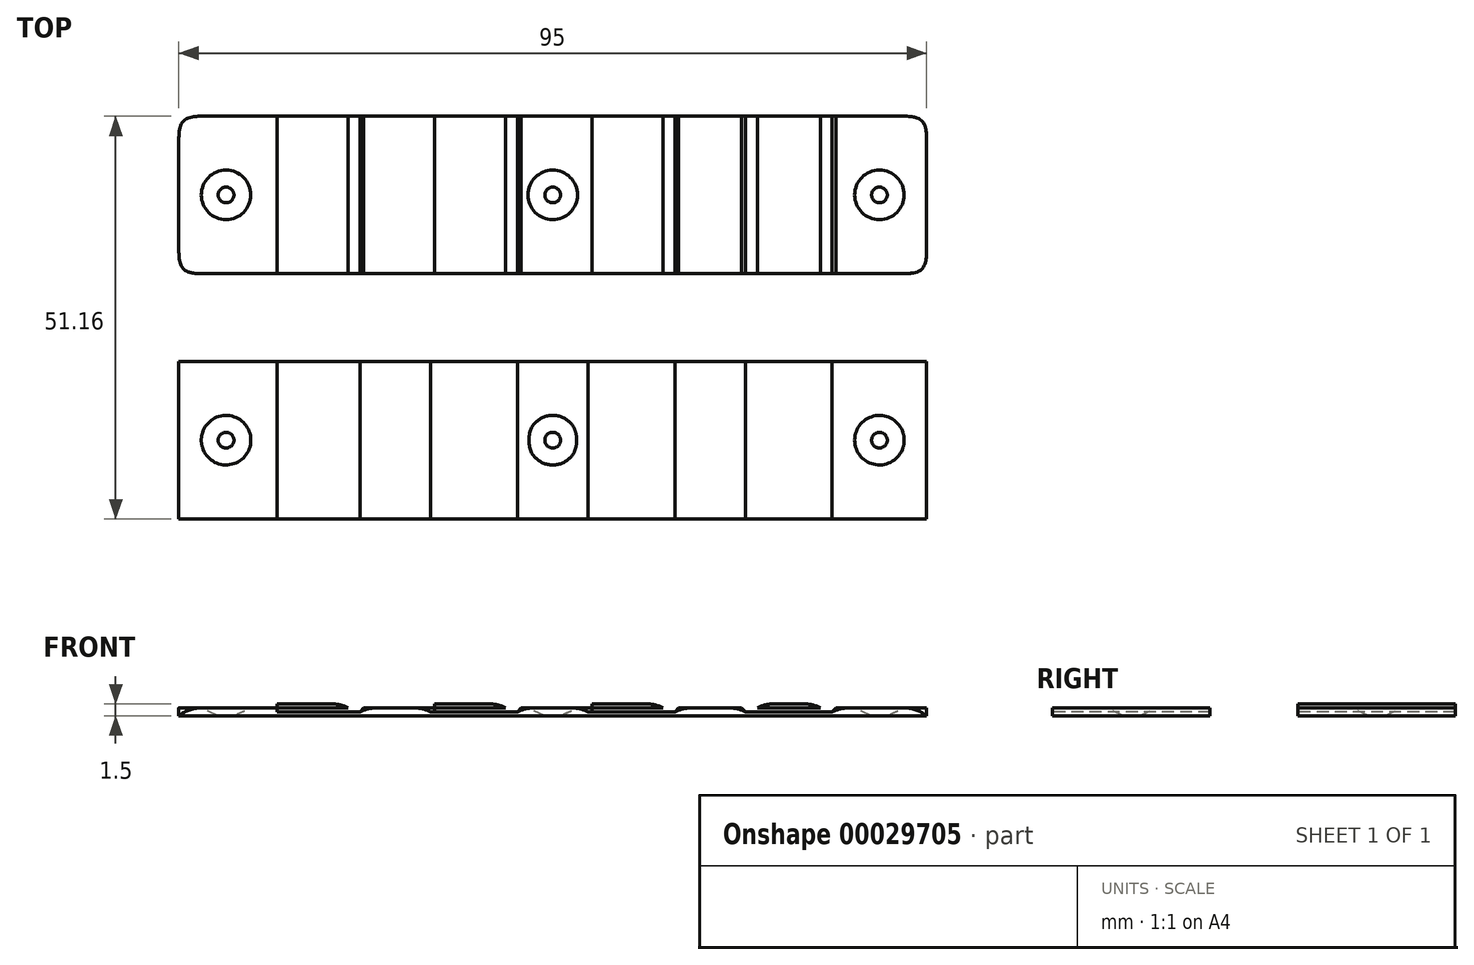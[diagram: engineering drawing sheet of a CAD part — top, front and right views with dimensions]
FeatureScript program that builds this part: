
annotation { "Feature Type Name" : "Feature", "Feature Type Description" : "" }
export const myFeature = defineFeature(function(context is Context, id is Id, definition is map)
    precondition{}
    {
        {
            var Q0;
            Q0=qCreatedBy(makeId("Top.planeOp"),FACE);
            var sketch = newSketch(context, id + "F0", { "sketchPlane" : qUnion([Q0])});
            skLineSegment(sketch, "E0.rect.bottom", {"start": v(47.5, 10) * mm, "end": v(-47.5, 10) * mm});
            skLineSegment(sketch, "E0.rect.top", {"start": v(47.5, -10) * mm, "end": v(-47.5, -10) * mm});
            skLineSegment(sketch, "E0.rect.left", {"start": v(47.5, 10) * mm, "end": v(47.5, -10) * mm});
            skLineSegment(sketch, "E0.rect.right", {"start": v(-47.5, 10) * mm, "end": v(-47.5, -10) * mm});
            skPoint(sketch, "E0.rect.middle", {"position": v(0, 0) * mm});
            skLineSegment(sketch, "E1.bottom", {"start": v(47.5, -21.16) * mm, "end": v(-47.5, -21.16) * mm});
            skLineSegment(sketch, "E1.top", {"start": v(47.5, -41.16) * mm, "end": v(-47.5, -41.16) * mm});
            skLineSegment(sketch, "E1.left", {"start": v(47.5, -21.16) * mm, "end": v(47.5, -41.16) * mm});
            skLineSegment(sketch, "E1.right", {"start": v(-47.5, -21.16) * mm, "end": v(-47.5, -41.16) * mm});
            skCircle(sketch, "E2", {"center": v(0, 0) * mm, "radius": 1 * mm});
            skCircle(sketch, "E3", {"center": v(0, -31.16) * mm, "radius": 1 * mm});
            skPoint(sketch, "E3.centerSnap0", {"position": v(47.5, -31.16) * mm});
            skPoint(sketch, "E3.centerSnap1", {"position": v(0, -41.16) * mm});
            skCircle(sketch, "E4", {"center": v(41.5, 0) * mm, "radius": 1 * mm});
            skCircle(sketch, "E5", {"center": v(41.5, -31.16) * mm, "radius": 1 * mm});
            skCircle(sketch, "E6", {"center": v(-41.5, 0) * mm, "radius": 1 * mm});
            skCircle(sketch, "E7", {"center": v(-41.5, -31.16) * mm, "radius": 1 * mm});
            skPoint(sketch, "E7.centerSnap0", {"position": v(-47.5, -31.16) * mm});
            skSolve(sketch);
        }
        {
            var Q0;
            Q0 = qSketchRegion(id + "F0", true);
            extrude(context, id + "F1", {"entities" : qUnion([Q0]), "depth" : 1 * mm});
        }
        {
            var Q0;
            Q0=makeQuery(id+"F1.opExtrude","CAP_FACE",FACE,{"disambiguationData":[OSD([sQuery(id+"F0.wireOp",EDGE,"E0.rect.bottom"),sQuery(id+"F0.wireOp",EDGE,"E0.rect.top"),sQuery(id+"F0.wireOp",EDGE,"E0.rect.left"),sQuery(id+"F0.wireOp",EDGE,"E0.rect.right"),sQuery(id+"F0.wireOp",EDGE,"E2"),sQuery(id+"F0.wireOp",EDGE,"E4"),sQuery(id+"F0.wireOp",EDGE,"E6")])],"isStart":false});
            var sketch = newSketch(context, id + "F2", { "sketchPlane" : qUnion([Q0])});
            skLineSegment(sketch, "E8.rect.right", {"start": v(-5, 10) * mm, "end": v(-5, -10) * mm});
            skPoint(sketch, "E8.rect.middle", {"position": v(0, 0) * mm});
            skLineSegment(sketch, "E9.bottom", {"start": v(-5, 10) * mm, "end": v(-15, 10) * mm});
            skLineSegment(sketch, "E9.top", {"start": v(-5, -10) * mm, "end": v(-15, -10) * mm});
            skLineSegment(sketch, "E9.right", {"start": v(-15, 10) * mm, "end": v(-15, -10) * mm});
            skLineSegment(sketch, "E10.1.0.0", {"start": v(5, 10) * mm, "end": v(5, -10) * mm});
            skLineSegment(sketch, "E10.1.0.1", {"start": v(15, 10) * mm, "end": v(5, 10) * mm});
            skLineSegment(sketch, "E10.1.0.2", {"start": v(15, 10) * mm, "end": v(15, -10) * mm});
            skLineSegment(sketch, "E10.1.0.3", {"start": v(15, -10) * mm, "end": v(5, -10) * mm});
            skLineSegment(sketch, "E10.2.0.0", {"start": v(25, 10) * mm, "end": v(25, -10) * mm});
            skLineSegment(sketch, "E10.2.0.1", {"start": v(35, 10) * mm, "end": v(25, 10) * mm});
            skLineSegment(sketch, "E10.2.0.2", {"start": v(35, 10) * mm, "end": v(35, -10) * mm});
            skLineSegment(sketch, "E10.2.0.3", {"start": v(35, -10) * mm, "end": v(25, -10) * mm});
            skLineSegment(sketch, "E10.direction1", {"start": v(-15, -10) * mm, "end": v(5, -10) * mm, "construction": true});
            skLineSegment(sketch, "E11.1.0.0", {"start": v(-35, 10) * mm, "end": v(-35, -10) * mm});
            skLineSegment(sketch, "E11.1.0.1", {"start": v(-25, 10) * mm, "end": v(-35, 10) * mm});
            skLineSegment(sketch, "E11.1.0.2", {"start": v(-25, 10) * mm, "end": v(-25, -10) * mm});
            skLineSegment(sketch, "E11.1.0.3", {"start": v(-25, -10) * mm, "end": v(-35, -10) * mm});
            skLineSegment(sketch, "E11.direction1", {"start": v(-15, -10) * mm, "end": v(-35, -10) * mm, "construction": true});
            skLineSegment(sketch, "E12.bottom", {"start": v(-35, -20.93) * mm, "end": v(-25, -20.93) * mm});
            skLineSegment(sketch, "E12.top", {"start": v(-35, -41.22) * mm, "end": v(-25, -41.22) * mm});
            skLineSegment(sketch, "E12.left", {"start": v(-35, -20.93) * mm, "end": v(-35, -41.22) * mm});
            skLineSegment(sketch, "E12.right", {"start": v(-25, -20.93) * mm, "end": v(-25, -41.22) * mm});
            skLineSegment(sketch, "E13.bottom", {"start": v(-15, -21.08) * mm, "end": v(-5, -21.08) * mm});
            skLineSegment(sketch, "E13.top", {"start": v(-15, -41.22) * mm, "end": v(-5, -41.22) * mm});
            skLineSegment(sketch, "E13.left", {"start": v(-15, -21.08) * mm, "end": v(-15, -41.22) * mm});
            skLineSegment(sketch, "E13.right", {"start": v(-5, -21.08) * mm, "end": v(-5, -41.22) * mm});
            skLineSegment(sketch, "E14.bottom", {"start": v(5, -21.04) * mm, "end": v(15, -21.04) * mm});
            skLineSegment(sketch, "E14.top", {"start": v(5, -41.22) * mm, "end": v(15, -41.22) * mm});
            skLineSegment(sketch, "E14.left", {"start": v(5, -21.04) * mm, "end": v(5, -41.22) * mm});
            skLineSegment(sketch, "E14.right", {"start": v(15, -21.04) * mm, "end": v(15, -41.22) * mm});
            skLineSegment(sketch, "E15.bottom", {"start": v(25, -20.8) * mm, "end": v(35, -20.8) * mm});
            skLineSegment(sketch, "E15.top", {"start": v(25, -41.22) * mm, "end": v(35, -41.22) * mm});
            skLineSegment(sketch, "E15.left", {"start": v(25, -20.8) * mm, "end": v(25, -41.22) * mm});
            skLineSegment(sketch, "E15.right", {"start": v(35, -20.8) * mm, "end": v(35, -41.22) * mm});
            skSolve(sketch);
        }
        {
            var Q0;
            Q0=makeQuery(id+"F2.imprint","IMPRINT",FACE,{"disambiguationData":[TD([[makeQuery(id+"F2.imprint","IMPRINT",EDGE,{"derivedFrom":sQuery(id+"F2.wireOp",EDGE,"E8.rect.right")}),-1.0]])]});
            extrude(context, id + "F3", {"entities" : qUnion([Q0]), "operationType" : NewBodyOperationType.ADD, "depth" : .5 * mm});
        }
        {
            var Q0;
            Q0=makeQuery(id+"F2.imprint","IMPRINT",FACE,{"disambiguationData":[TD([[makeQuery(id+"F2.imprint","IMPRINT",EDGE,{"derivedFrom":sQuery(id+"F2.wireOp",EDGE,"E11.1.0.0")}),1.0]])]});
            var Q1;
            Q1=makeQuery(id+"F2.imprint","IMPRINT",FACE,{"disambiguationData":[TD([[makeQuery(id+"F2.imprint","IMPRINT",EDGE,{"derivedFrom":sQuery(id+"F2.wireOp",EDGE,"E10.1.0.0")}),1.0]])]});
            var Q2;
            Q2=makeQuery(id+"F2.imprint","IMPRINT",FACE,{"disambiguationData":[TD([[makeQuery(id+"F2.imprint","IMPRINT",EDGE,{"derivedFrom":sQuery(id+"F2.wireOp",EDGE,"E10.2.0.0")}),1.0]])]});
            extrude(context, id + "F4", {"entities" : qUnion([Q0, Q1, Q2]), "operationType" : NewBodyOperationType.ADD, "depth" : .5 * mm});
        }
        {
            var Q0;
            Q0 = qSketchRegion(id + "F2", true);
            extrude(context, id + "F5", {"entities" : qUnion([Q0]), "operationType" : NewBodyOperationType.REMOVE, "oppositeDirection" : true, "depth" : .5 * mm});
        }
        {
            var Q0;
            Q0=makeQuery(id+"F4.opExtrude","CAP_EDGE",EDGE,{"disambiguationData":[OSD([sQuery(id+"F2.wireOp",EDGE,"E10.2.0.2")])],"isStart":true});
            var Q1;
            Q1=makeQuery(id+"F4.opExtrude","CAP_EDGE",EDGE,{"disambiguationData":[OSD([sQuery(id+"F2.wireOp",EDGE,"E10.1.0.2")])],"isStart":true});
            var Q2;
            Q2=makeQuery(id+"F3.opExtrude","CAP_EDGE",EDGE,{"disambiguationData":[OSD([sQuery(id+"F2.wireOp",EDGE,"E8.rect.right")])],"isStart":true});
            var Q3;
            Q3=makeQuery(id+"F4.opExtrude","CAP_EDGE",EDGE,{"disambiguationData":[OSD([sQuery(id+"F2.wireOp",EDGE,"E11.1.0.2")])],"isStart":true});
            var Q4;
            Q4=makeQuery(id+"F4.opExtrude","CAP_EDGE",EDGE,{"disambiguationData":[OSD([sQuery(id+"F2.wireOp",EDGE,"E11.1.0.0")])],"isStart":true});
            var Q5;
            Q5=makeQuery(id+"F3.opExtrude","CAP_EDGE",EDGE,{"disambiguationData":[OSD([sQuery(id+"F2.wireOp",EDGE,"E9.right")])],"isStart":true});
            var Q6;
            Q6=makeQuery(id+"F4.opExtrude","CAP_EDGE",EDGE,{"disambiguationData":[OSD([sQuery(id+"F2.wireOp",EDGE,"E10.1.0.0")])],"isStart":true});
            var Q7;
            Q7=makeQuery(id+"F4.opExtrude","CAP_EDGE",EDGE,{"disambiguationData":[OSD([sQuery(id+"F2.wireOp",EDGE,"E10.2.0.0")])],"isStart":true});
            var Q8;
            Q8=makeQuery(id+"F5.boolean.opBoolean","COPY",EDGE,{"derivedFrom":makeQuery(id+"F5.opExtrude","CAP_EDGE",EDGE,{"disambiguationData":[OSD([sQuery(id+"F2.wireOp",EDGE,"E12.left")])],"isStart":true})});
            var Q9;
            Q9=makeQuery(id+"F5.boolean.opBoolean","COPY",EDGE,{"derivedFrom":makeQuery(id+"F5.opExtrude","CAP_EDGE",EDGE,{"disambiguationData":[OSD([sQuery(id+"F2.wireOp",EDGE,"E12.right")])],"isStart":true})});
            var Q10;
            Q10=makeQuery(id+"F5.boolean.opBoolean","COPY",EDGE,{"derivedFrom":makeQuery(id+"F5.opExtrude","CAP_EDGE",EDGE,{"disambiguationData":[OSD([sQuery(id+"F2.wireOp",EDGE,"E13.left")])],"isStart":true})});
            var Q11;
            Q11=makeQuery(id+"F5.boolean.opBoolean","COPY",EDGE,{"derivedFrom":makeQuery(id+"F5.opExtrude","CAP_EDGE",EDGE,{"disambiguationData":[OSD([sQuery(id+"F2.wireOp",EDGE,"E13.right")])],"isStart":true})});
            var Q12;
            Q12=makeQuery(id+"F5.boolean.opBoolean","COPY",EDGE,{"derivedFrom":makeQuery(id+"F5.opExtrude","CAP_EDGE",EDGE,{"disambiguationData":[OSD([sQuery(id+"F2.wireOp",EDGE,"E14.left")])],"isStart":true})});
            var Q13;
            Q13=makeQuery(id+"F5.boolean.opBoolean","COPY",EDGE,{"derivedFrom":makeQuery(id+"F5.opExtrude","CAP_EDGE",EDGE,{"disambiguationData":[OSD([sQuery(id+"F2.wireOp",EDGE,"E14.right")])],"isStart":true})});
            var Q14;
            Q14=makeQuery(id+"F5.boolean.opBoolean","COPY",EDGE,{"derivedFrom":makeQuery(id+"F5.opExtrude","CAP_EDGE",EDGE,{"disambiguationData":[OSD([sQuery(id+"F2.wireOp",EDGE,"E15.left")])],"isStart":true})});
            var Q15;
            Q15=makeQuery(id+"F5.boolean.opBoolean","COPY",EDGE,{"derivedFrom":makeQuery(id+"F5.opExtrude","CAP_EDGE",EDGE,{"disambiguationData":[OSD([sQuery(id+"F2.wireOp",EDGE,"E15.right")])],"isStart":true})});
            var Q16;
            Q16=makeQuery(id+"F1.opExtrude","CAP_EDGE",EDGE,{"disambiguationData":[OSD([sQuery(id+"F0.wireOp",EDGE,"E1.right")])],"isStart":false});
            var Q17;
            Q17=makeQuery(id+"F1.opExtrude","CAP_EDGE",EDGE,{"disambiguationData":[OSD([sQuery(id+"F0.wireOp",EDGE,"E1.left")])],"isStart":false});
            chamfer(context, id + "F6", {"entities" : qUnion([Q0, Q1, Q2, Q3, Q4, Q5, Q6, Q7, Q8, Q9, Q10, Q11, Q12, Q13, Q14, Q15, Q16, Q17]), "width" : 1 * mm, "tangentPropagation" : true});
        }
        {
            var Q0;
            Q0=makeQuery(id+"F1.opExtrude","SWEPT_EDGE",EDGE,{"disambiguationData":[OSD([sQuery(id+"F0.wireOp",EDGE,"E0.rect.bottom"),sQuery(id+"F0.wireOp",EDGE,"E0.rect.left")])]});
            var Q1;
            Q1=makeQuery(id+"F1.opExtrude","SWEPT_EDGE",EDGE,{"disambiguationData":[OSD([sQuery(id+"F0.wireOp",EDGE,"E0.rect.top"),sQuery(id+"F0.wireOp",EDGE,"E0.rect.left")])]});
            var Q2;
            Q2=makeQuery(id+"F1.opExtrude","SWEPT_EDGE",EDGE,{"disambiguationData":[OSD([sQuery(id+"F0.wireOp",EDGE,"E1.bottom"),sQuery(id+"F0.wireOp",EDGE,"E1.left")])]});
            var Q3;
            Q3=makeQuery(id+"F1.opExtrude","SWEPT_EDGE",EDGE,{"disambiguationData":[OSD([sQuery(id+"F0.wireOp",EDGE,"E0.rect.bottom"),sQuery(id+"F0.wireOp",EDGE,"E0.rect.right")])]});
            var Q4;
            Q4=makeQuery(id+"F1.opExtrude","SWEPT_EDGE",EDGE,{"disambiguationData":[OSD([sQuery(id+"F0.wireOp",EDGE,"E0.rect.top"),sQuery(id+"F0.wireOp",EDGE,"E0.rect.right")])]});
            var Q5;
            Q5=makeQuery(id+"F1.opExtrude","SWEPT_EDGE",EDGE,{"disambiguationData":[OSD([sQuery(id+"F0.wireOp",EDGE,"E1.bottom"),sQuery(id+"F0.wireOp",EDGE,"E1.right")])]});
            var Q6;
            Q6=makeQuery(id+"F1.opExtrude","SWEPT_EDGE",EDGE,{"disambiguationData":[OSD([sQuery(id+"F0.wireOp",EDGE,"E1.top"),sQuery(id+"F0.wireOp",EDGE,"E1.right")])]});
            var Q7;
            Q7=makeQuery(id+"F1.opExtrude","SWEPT_EDGE",EDGE,{"disambiguationData":[OSD([sQuery(id+"F0.wireOp",EDGE,"E1.top"),sQuery(id+"F0.wireOp",EDGE,"E1.left")])]});
            fillet(context, id + "F7", {"entities" : qUnion([Q0, Q1, Q2, Q3, Q4, Q5, Q6, Q7]), "radius" : 3 * mm, "tangentPropagation" : true, "rho" : 0.6, "crossSection" : FilletCrossSection.CONIC, "allowEdgeOverflow" : false});
        }
        {
            var Q0;
            Q0=makeQuery(id+"F1.opExtrude","CAP_EDGE",EDGE,{"disambiguationData":[OSD([sQuery(id+"F0.wireOp",EDGE,"E6")])],"isStart":false});
            var Q1;
            Q1=makeQuery(id+"F1.opExtrude","CAP_EDGE",EDGE,{"disambiguationData":[OSD([sQuery(id+"F0.wireOp",EDGE,"E2")])],"isStart":false});
            var Q2;
            Q2=makeQuery(id+"F1.opExtrude","CAP_EDGE",EDGE,{"disambiguationData":[OSD([sQuery(id+"F0.wireOp",EDGE,"E4")])],"isStart":false});
            var Q3;
            Q3=makeQuery(id+"F1.opExtrude","CAP_EDGE",EDGE,{"disambiguationData":[OSD([sQuery(id+"F0.wireOp",EDGE,"E7")])],"isStart":false});
            var Q4;
            Q4=makeQuery(id+"F1.opExtrude","CAP_EDGE",EDGE,{"disambiguationData":[OSD([sQuery(id+"F0.wireOp",EDGE,"E3")])],"isStart":false});
            var Q5;
            Q5=makeQuery(id+"F1.opExtrude","CAP_EDGE",EDGE,{"disambiguationData":[OSD([sQuery(id+"F0.wireOp",EDGE,"E5")])],"isStart":false});
            chamfer(context, id + "F8", {"entities" : qUnion([Q0, Q1, Q2, Q3, Q4, Q5]), "chamferType" : ChamferType.OFFSET_ANGLE, "width" : 1 * mm, "oppositeDirection" : false, "angle" : 65 * degree, "tangentPropagation" : true});
        }
        {
            var Q0;
            {var subQ0=sQuery(id+"F2.wireOp",EDGE,"E11.1.0.0");Q0=makeQuery(id+"F6.opChamfer","BLEND_EDGE",EDGE,{"blendedFrom":[makeQuery(id+"F4.opExtrude","CAP_EDGE",EDGE,{"disambiguationData":[OSD([subQ0])],"isStart":true}),makeQuery(id+"F4.opExtrude","CAP_FACE",FACE,{"disambiguationData":[OSD([subQ0,sQuery(id+"F2.wireOp",EDGE,"E11.1.0.1"),sQuery(id+"F2.wireOp",EDGE,"E11.1.0.2"),sQuery(id+"F2.wireOp",EDGE,"E11.1.0.3")])],"isStart":false})],"blendedInto":[makeQuery(id+"F4.opExtrude","CAP_FACE",FACE,{"disambiguationData":[OSD([subQ0,sQuery(id+"F2.wireOp",EDGE,"E11.1.0.1"),sQuery(id+"F2.wireOp",EDGE,"E11.1.0.2"),sQuery(id+"F2.wireOp",EDGE,"E11.1.0.3")])],"isStart":false})]});}
            var Q1;
            {var subQ0=sQuery(id+"F2.wireOp",EDGE,"E11.1.0.2");Q1=makeQuery(id+"F6.opChamfer","BLEND_EDGE",EDGE,{"blendedFrom":[makeQuery(id+"F4.opExtrude","CAP_EDGE",EDGE,{"disambiguationData":[OSD([subQ0])],"isStart":true}),makeQuery(id+"F4.opExtrude","CAP_FACE",FACE,{"disambiguationData":[OSD([sQuery(id+"F2.wireOp",EDGE,"E11.1.0.0"),sQuery(id+"F2.wireOp",EDGE,"E11.1.0.1"),subQ0,sQuery(id+"F2.wireOp",EDGE,"E11.1.0.3")])],"isStart":false})],"blendedInto":[makeQuery(id+"F4.opExtrude","CAP_FACE",FACE,{"disambiguationData":[OSD([sQuery(id+"F2.wireOp",EDGE,"E11.1.0.0"),sQuery(id+"F2.wireOp",EDGE,"E11.1.0.1"),subQ0,sQuery(id+"F2.wireOp",EDGE,"E11.1.0.3")])],"isStart":false})]});}
            var Q2;
            {var subQ0=sQuery(id+"F2.wireOp",EDGE,"E9.right");Q2=makeQuery(id+"F6.opChamfer","BLEND_EDGE",EDGE,{"blendedFrom":[makeQuery(id+"F3.opExtrude","CAP_EDGE",EDGE,{"disambiguationData":[OSD([subQ0])],"isStart":true}),makeQuery(id+"F3.opExtrude","CAP_FACE",FACE,{"disambiguationData":[OSD([sQuery(id+"F2.wireOp",EDGE,"E8.rect.right"),sQuery(id+"F2.wireOp",EDGE,"E9.bottom"),sQuery(id+"F2.wireOp",EDGE,"E9.top"),subQ0])],"isStart":false})],"blendedInto":[makeQuery(id+"F3.opExtrude","CAP_FACE",FACE,{"disambiguationData":[OSD([sQuery(id+"F2.wireOp",EDGE,"E8.rect.right"),sQuery(id+"F2.wireOp",EDGE,"E9.bottom"),sQuery(id+"F2.wireOp",EDGE,"E9.top"),subQ0])],"isStart":false})]});}
            var Q3;
            {var subQ0=sQuery(id+"F2.wireOp",EDGE,"E8.rect.right");Q3=makeQuery(id+"F6.opChamfer","BLEND_EDGE",EDGE,{"blendedFrom":[makeQuery(id+"F3.opExtrude","CAP_EDGE",EDGE,{"disambiguationData":[OSD([subQ0])],"isStart":true}),makeQuery(id+"F3.opExtrude","CAP_FACE",FACE,{"disambiguationData":[OSD([subQ0,sQuery(id+"F2.wireOp",EDGE,"E9.bottom"),sQuery(id+"F2.wireOp",EDGE,"E9.top"),sQuery(id+"F2.wireOp",EDGE,"E9.right")])],"isStart":false})],"blendedInto":[makeQuery(id+"F3.opExtrude","CAP_FACE",FACE,{"disambiguationData":[OSD([subQ0,sQuery(id+"F2.wireOp",EDGE,"E9.bottom"),sQuery(id+"F2.wireOp",EDGE,"E9.top"),sQuery(id+"F2.wireOp",EDGE,"E9.right")])],"isStart":false})]});}
            var Q4;
            {var subQ0=sQuery(id+"F2.wireOp",EDGE,"E10.1.0.0");Q4=makeQuery(id+"F6.opChamfer","BLEND_EDGE",EDGE,{"blendedFrom":[makeQuery(id+"F4.opExtrude","CAP_EDGE",EDGE,{"disambiguationData":[OSD([subQ0])],"isStart":true}),makeQuery(id+"F4.opExtrude","CAP_FACE",FACE,{"disambiguationData":[OSD([subQ0,sQuery(id+"F2.wireOp",EDGE,"E10.1.0.1"),sQuery(id+"F2.wireOp",EDGE,"E10.1.0.2"),sQuery(id+"F2.wireOp",EDGE,"E10.1.0.3")])],"isStart":false})],"blendedInto":[makeQuery(id+"F4.opExtrude","CAP_FACE",FACE,{"disambiguationData":[OSD([subQ0,sQuery(id+"F2.wireOp",EDGE,"E10.1.0.1"),sQuery(id+"F2.wireOp",EDGE,"E10.1.0.2"),sQuery(id+"F2.wireOp",EDGE,"E10.1.0.3")])],"isStart":false})]});}
            var Q5;
            {var subQ0=sQuery(id+"F2.wireOp",EDGE,"E10.1.0.2");Q5=makeQuery(id+"F6.opChamfer","BLEND_EDGE",EDGE,{"blendedFrom":[makeQuery(id+"F4.opExtrude","CAP_EDGE",EDGE,{"disambiguationData":[OSD([subQ0])],"isStart":true}),makeQuery(id+"F4.opExtrude","CAP_FACE",FACE,{"disambiguationData":[OSD([sQuery(id+"F2.wireOp",EDGE,"E10.1.0.0"),sQuery(id+"F2.wireOp",EDGE,"E10.1.0.1"),subQ0,sQuery(id+"F2.wireOp",EDGE,"E10.1.0.3")])],"isStart":false})],"blendedInto":[makeQuery(id+"F4.opExtrude","CAP_FACE",FACE,{"disambiguationData":[OSD([sQuery(id+"F2.wireOp",EDGE,"E10.1.0.0"),sQuery(id+"F2.wireOp",EDGE,"E10.1.0.1"),subQ0,sQuery(id+"F2.wireOp",EDGE,"E10.1.0.3")])],"isStart":false})]});}
            var Q6;
            {var subQ0=sQuery(id+"F2.wireOp",EDGE,"E10.2.0.0");Q6=makeQuery(id+"F6.opChamfer","BLEND_EDGE",EDGE,{"blendedFrom":[makeQuery(id+"F4.opExtrude","CAP_EDGE",EDGE,{"disambiguationData":[OSD([subQ0])],"isStart":true}),makeQuery(id+"F4.opExtrude","CAP_FACE",FACE,{"disambiguationData":[OSD([subQ0,sQuery(id+"F2.wireOp",EDGE,"E10.2.0.1"),sQuery(id+"F2.wireOp",EDGE,"E10.2.0.2"),sQuery(id+"F2.wireOp",EDGE,"E10.2.0.3")])],"isStart":false})],"blendedInto":[makeQuery(id+"F4.opExtrude","CAP_FACE",FACE,{"disambiguationData":[OSD([subQ0,sQuery(id+"F2.wireOp",EDGE,"E10.2.0.1"),sQuery(id+"F2.wireOp",EDGE,"E10.2.0.2"),sQuery(id+"F2.wireOp",EDGE,"E10.2.0.3")])],"isStart":false})]});}
            var Q7;
            {var subQ0=sQuery(id+"F2.wireOp",EDGE,"E10.2.0.2");Q7=makeQuery(id+"F6.opChamfer","BLEND_EDGE",EDGE,{"blendedFrom":[makeQuery(id+"F4.opExtrude","CAP_EDGE",EDGE,{"disambiguationData":[OSD([subQ0])],"isStart":true}),makeQuery(id+"F4.opExtrude","CAP_FACE",FACE,{"disambiguationData":[OSD([sQuery(id+"F2.wireOp",EDGE,"E10.2.0.0"),sQuery(id+"F2.wireOp",EDGE,"E10.2.0.1"),subQ0,sQuery(id+"F2.wireOp",EDGE,"E10.2.0.3")])],"isStart":false})],"blendedInto":[makeQuery(id+"F4.opExtrude","CAP_FACE",FACE,{"disambiguationData":[OSD([sQuery(id+"F2.wireOp",EDGE,"E10.2.0.0"),sQuery(id+"F2.wireOp",EDGE,"E10.2.0.1"),subQ0,sQuery(id+"F2.wireOp",EDGE,"E10.2.0.3")])],"isStart":false})]});}
            var Q8;
            {var subQ0=sQuery(id+"F2.wireOp",EDGE,"E15.right");var subQ1=sQuery(id+"F0.wireOp",EDGE,"E1.bottom");var subQ2=sQuery(id+"F0.wireOp",EDGE,"E1.top");var subQ3=sQuery(id+"F0.wireOp",EDGE,"E1.left");var subQ4=sQuery(id+"F0.wireOp",EDGE,"E5");Q8=makeQuery(id+"F6.opChamfer","BLEND_EDGE",EDGE,{"blendedFrom":[makeQuery(id+"F5.boolean.opBoolean","COPY",EDGE,{"derivedFrom":makeQuery(id+"F5.opExtrude","CAP_EDGE",EDGE,{"disambiguationData":[OSD([subQ0])],"isStart":true})}),makeQuery(id+"F5.boolean.opBoolean","SPLIT",FACE,{"disambiguationData":[TD([makeQuery(id+"F1.opExtrude","SWEPT_FACE",FACE,{"disambiguationData":[OSD([subQ3])]})])],"derivedFrom":makeQuery(id+"F1.opExtrude","CAP_FACE",FACE,{"disambiguationData":[OSD([subQ1,subQ2,subQ3,sQuery(id+"F0.wireOp",EDGE,"E1.right"),sQuery(id+"F0.wireOp",EDGE,"E3"),subQ4,sQuery(id+"F0.wireOp",EDGE,"E7")])],"isStart":false})})],"blendedInto":[makeQuery(id+"F5.boolean.opBoolean","SPLIT",FACE,{"disambiguationData":[TD([makeQuery(id+"F1.opExtrude","SWEPT_FACE",FACE,{"disambiguationData":[OSD([subQ3])]})])],"derivedFrom":makeQuery(id+"F1.opExtrude","CAP_FACE",FACE,{"disambiguationData":[OSD([subQ1,subQ2,subQ3,sQuery(id+"F0.wireOp",EDGE,"E1.right"),sQuery(id+"F0.wireOp",EDGE,"E3"),subQ4,sQuery(id+"F0.wireOp",EDGE,"E7")])],"isStart":false})})]});}
            var Q9;
            {var subQ0=sQuery(id+"F2.wireOp",EDGE,"E15.left");var subQ1=sQuery(id+"F0.wireOp",EDGE,"E1.bottom");var subQ2=sQuery(id+"F0.wireOp",EDGE,"E1.top");Q9=makeQuery(id+"F6.opChamfer","BLEND_EDGE",EDGE,{"blendedFrom":[makeQuery(id+"F5.boolean.opBoolean","COPY",EDGE,{"derivedFrom":makeQuery(id+"F5.opExtrude","CAP_EDGE",EDGE,{"disambiguationData":[OSD([subQ0])],"isStart":true})}),makeQuery(id+"F5.boolean.opBoolean","SPLIT",FACE,{"disambiguationData":[TD([makeQuery(id+"F5.opExtrude","SWEPT_FACE",FACE,{"disambiguationData":[OSD([sQuery(id+"F2.wireOp",EDGE,"E14.right")])]})])],"derivedFrom":makeQuery(id+"F1.opExtrude","CAP_FACE",FACE,{"disambiguationData":[OSD([subQ1,subQ2,sQuery(id+"F0.wireOp",EDGE,"E1.left"),sQuery(id+"F0.wireOp",EDGE,"E1.right"),sQuery(id+"F0.wireOp",EDGE,"E3"),sQuery(id+"F0.wireOp",EDGE,"E5"),sQuery(id+"F0.wireOp",EDGE,"E7")])],"isStart":false})})],"blendedInto":[makeQuery(id+"F5.boolean.opBoolean","SPLIT",FACE,{"disambiguationData":[TD([makeQuery(id+"F5.opExtrude","SWEPT_FACE",FACE,{"disambiguationData":[OSD([sQuery(id+"F2.wireOp",EDGE,"E14.right")])]})])],"derivedFrom":makeQuery(id+"F1.opExtrude","CAP_FACE",FACE,{"disambiguationData":[OSD([subQ1,subQ2,sQuery(id+"F0.wireOp",EDGE,"E1.left"),sQuery(id+"F0.wireOp",EDGE,"E1.right"),sQuery(id+"F0.wireOp",EDGE,"E3"),sQuery(id+"F0.wireOp",EDGE,"E5"),sQuery(id+"F0.wireOp",EDGE,"E7")])],"isStart":false})})]});}
            var Q10;
            {var subQ0=sQuery(id+"F2.wireOp",EDGE,"E14.right");var subQ1=sQuery(id+"F0.wireOp",EDGE,"E1.bottom");var subQ2=sQuery(id+"F0.wireOp",EDGE,"E1.top");Q10=makeQuery(id+"F6.opChamfer","BLEND_EDGE",EDGE,{"blendedFrom":[makeQuery(id+"F5.boolean.opBoolean","COPY",EDGE,{"derivedFrom":makeQuery(id+"F5.opExtrude","CAP_EDGE",EDGE,{"disambiguationData":[OSD([subQ0])],"isStart":true})}),makeQuery(id+"F5.boolean.opBoolean","SPLIT",FACE,{"disambiguationData":[TD([makeQuery(id+"F5.opExtrude","SWEPT_FACE",FACE,{"disambiguationData":[OSD([subQ0])]})])],"derivedFrom":makeQuery(id+"F1.opExtrude","CAP_FACE",FACE,{"disambiguationData":[OSD([subQ1,subQ2,sQuery(id+"F0.wireOp",EDGE,"E1.left"),sQuery(id+"F0.wireOp",EDGE,"E1.right"),sQuery(id+"F0.wireOp",EDGE,"E3"),sQuery(id+"F0.wireOp",EDGE,"E5"),sQuery(id+"F0.wireOp",EDGE,"E7")])],"isStart":false})})],"blendedInto":[makeQuery(id+"F5.boolean.opBoolean","SPLIT",FACE,{"disambiguationData":[TD([makeQuery(id+"F5.opExtrude","SWEPT_FACE",FACE,{"disambiguationData":[OSD([subQ0])]})])],"derivedFrom":makeQuery(id+"F1.opExtrude","CAP_FACE",FACE,{"disambiguationData":[OSD([subQ1,subQ2,sQuery(id+"F0.wireOp",EDGE,"E1.left"),sQuery(id+"F0.wireOp",EDGE,"E1.right"),sQuery(id+"F0.wireOp",EDGE,"E3"),sQuery(id+"F0.wireOp",EDGE,"E5"),sQuery(id+"F0.wireOp",EDGE,"E7")])],"isStart":false})})]});}
            var Q11;
            {var subQ0=sQuery(id+"F2.wireOp",EDGE,"E14.left");var subQ1=sQuery(id+"F0.wireOp",EDGE,"E1.bottom");var subQ2=sQuery(id+"F0.wireOp",EDGE,"E1.top");var subQ3=sQuery(id+"F0.wireOp",EDGE,"E3");Q11=makeQuery(id+"F6.opChamfer","BLEND_EDGE",EDGE,{"blendedFrom":[makeQuery(id+"F5.boolean.opBoolean","COPY",EDGE,{"derivedFrom":makeQuery(id+"F5.opExtrude","CAP_EDGE",EDGE,{"disambiguationData":[OSD([subQ0])],"isStart":true})}),makeQuery(id+"F5.boolean.opBoolean","SPLIT",FACE,{"disambiguationData":[TD([makeQuery(id+"F1.opExtrude","SWEPT_FACE",FACE,{"disambiguationData":[OSD([subQ3])]})])],"derivedFrom":makeQuery(id+"F1.opExtrude","CAP_FACE",FACE,{"disambiguationData":[OSD([subQ1,subQ2,sQuery(id+"F0.wireOp",EDGE,"E1.left"),sQuery(id+"F0.wireOp",EDGE,"E1.right"),subQ3,sQuery(id+"F0.wireOp",EDGE,"E5"),sQuery(id+"F0.wireOp",EDGE,"E7")])],"isStart":false})})],"blendedInto":[makeQuery(id+"F5.boolean.opBoolean","SPLIT",FACE,{"disambiguationData":[TD([makeQuery(id+"F1.opExtrude","SWEPT_FACE",FACE,{"disambiguationData":[OSD([subQ3])]})])],"derivedFrom":makeQuery(id+"F1.opExtrude","CAP_FACE",FACE,{"disambiguationData":[OSD([subQ1,subQ2,sQuery(id+"F0.wireOp",EDGE,"E1.left"),sQuery(id+"F0.wireOp",EDGE,"E1.right"),subQ3,sQuery(id+"F0.wireOp",EDGE,"E5"),sQuery(id+"F0.wireOp",EDGE,"E7")])],"isStart":false})})]});}
            var Q12;
            {var subQ0=sQuery(id+"F2.wireOp",EDGE,"E13.right");var subQ1=sQuery(id+"F0.wireOp",EDGE,"E1.bottom");var subQ2=sQuery(id+"F0.wireOp",EDGE,"E1.top");var subQ3=sQuery(id+"F0.wireOp",EDGE,"E3");Q12=makeQuery(id+"F6.opChamfer","BLEND_EDGE",EDGE,{"blendedFrom":[makeQuery(id+"F5.boolean.opBoolean","COPY",EDGE,{"derivedFrom":makeQuery(id+"F5.opExtrude","CAP_EDGE",EDGE,{"disambiguationData":[OSD([subQ0])],"isStart":true})}),makeQuery(id+"F5.boolean.opBoolean","SPLIT",FACE,{"disambiguationData":[TD([makeQuery(id+"F1.opExtrude","SWEPT_FACE",FACE,{"disambiguationData":[OSD([subQ3])]})])],"derivedFrom":makeQuery(id+"F1.opExtrude","CAP_FACE",FACE,{"disambiguationData":[OSD([subQ1,subQ2,sQuery(id+"F0.wireOp",EDGE,"E1.left"),sQuery(id+"F0.wireOp",EDGE,"E1.right"),subQ3,sQuery(id+"F0.wireOp",EDGE,"E5"),sQuery(id+"F0.wireOp",EDGE,"E7")])],"isStart":false})})],"blendedInto":[makeQuery(id+"F5.boolean.opBoolean","SPLIT",FACE,{"disambiguationData":[TD([makeQuery(id+"F1.opExtrude","SWEPT_FACE",FACE,{"disambiguationData":[OSD([subQ3])]})])],"derivedFrom":makeQuery(id+"F1.opExtrude","CAP_FACE",FACE,{"disambiguationData":[OSD([subQ1,subQ2,sQuery(id+"F0.wireOp",EDGE,"E1.left"),sQuery(id+"F0.wireOp",EDGE,"E1.right"),subQ3,sQuery(id+"F0.wireOp",EDGE,"E5"),sQuery(id+"F0.wireOp",EDGE,"E7")])],"isStart":false})})]});}
            var Q13;
            {var subQ0=sQuery(id+"F2.wireOp",EDGE,"E13.left");var subQ1=sQuery(id+"F0.wireOp",EDGE,"E1.bottom");var subQ2=sQuery(id+"F0.wireOp",EDGE,"E1.top");Q13=makeQuery(id+"F6.opChamfer","BLEND_EDGE",EDGE,{"blendedFrom":[makeQuery(id+"F5.boolean.opBoolean","COPY",EDGE,{"derivedFrom":makeQuery(id+"F5.opExtrude","CAP_EDGE",EDGE,{"disambiguationData":[OSD([subQ0])],"isStart":true})}),makeQuery(id+"F5.boolean.opBoolean","SPLIT",FACE,{"disambiguationData":[TD([makeQuery(id+"F5.opExtrude","SWEPT_FACE",FACE,{"disambiguationData":[OSD([sQuery(id+"F2.wireOp",EDGE,"E12.right")])]})])],"derivedFrom":makeQuery(id+"F1.opExtrude","CAP_FACE",FACE,{"disambiguationData":[OSD([subQ1,subQ2,sQuery(id+"F0.wireOp",EDGE,"E1.left"),sQuery(id+"F0.wireOp",EDGE,"E1.right"),sQuery(id+"F0.wireOp",EDGE,"E3"),sQuery(id+"F0.wireOp",EDGE,"E5"),sQuery(id+"F0.wireOp",EDGE,"E7")])],"isStart":false})})],"blendedInto":[makeQuery(id+"F5.boolean.opBoolean","SPLIT",FACE,{"disambiguationData":[TD([makeQuery(id+"F5.opExtrude","SWEPT_FACE",FACE,{"disambiguationData":[OSD([sQuery(id+"F2.wireOp",EDGE,"E12.right")])]})])],"derivedFrom":makeQuery(id+"F1.opExtrude","CAP_FACE",FACE,{"disambiguationData":[OSD([subQ1,subQ2,sQuery(id+"F0.wireOp",EDGE,"E1.left"),sQuery(id+"F0.wireOp",EDGE,"E1.right"),sQuery(id+"F0.wireOp",EDGE,"E3"),sQuery(id+"F0.wireOp",EDGE,"E5"),sQuery(id+"F0.wireOp",EDGE,"E7")])],"isStart":false})})]});}
            var Q14;
            {var subQ0=sQuery(id+"F2.wireOp",EDGE,"E12.right");var subQ1=sQuery(id+"F0.wireOp",EDGE,"E1.bottom");var subQ2=sQuery(id+"F0.wireOp",EDGE,"E1.top");Q14=makeQuery(id+"F6.opChamfer","BLEND_EDGE",EDGE,{"blendedFrom":[makeQuery(id+"F5.boolean.opBoolean","COPY",EDGE,{"derivedFrom":makeQuery(id+"F5.opExtrude","CAP_EDGE",EDGE,{"disambiguationData":[OSD([subQ0])],"isStart":true})}),makeQuery(id+"F5.boolean.opBoolean","SPLIT",FACE,{"disambiguationData":[TD([makeQuery(id+"F5.opExtrude","SWEPT_FACE",FACE,{"disambiguationData":[OSD([subQ0])]})])],"derivedFrom":makeQuery(id+"F1.opExtrude","CAP_FACE",FACE,{"disambiguationData":[OSD([subQ1,subQ2,sQuery(id+"F0.wireOp",EDGE,"E1.left"),sQuery(id+"F0.wireOp",EDGE,"E1.right"),sQuery(id+"F0.wireOp",EDGE,"E3"),sQuery(id+"F0.wireOp",EDGE,"E5"),sQuery(id+"F0.wireOp",EDGE,"E7")])],"isStart":false})})],"blendedInto":[makeQuery(id+"F5.boolean.opBoolean","SPLIT",FACE,{"disambiguationData":[TD([makeQuery(id+"F5.opExtrude","SWEPT_FACE",FACE,{"disambiguationData":[OSD([subQ0])]})])],"derivedFrom":makeQuery(id+"F1.opExtrude","CAP_FACE",FACE,{"disambiguationData":[OSD([subQ1,subQ2,sQuery(id+"F0.wireOp",EDGE,"E1.left"),sQuery(id+"F0.wireOp",EDGE,"E1.right"),sQuery(id+"F0.wireOp",EDGE,"E3"),sQuery(id+"F0.wireOp",EDGE,"E5"),sQuery(id+"F0.wireOp",EDGE,"E7")])],"isStart":false})})]});}
            var Q15;
            {var subQ0=sQuery(id+"F2.wireOp",EDGE,"E12.left");var subQ1=sQuery(id+"F0.wireOp",EDGE,"E1.bottom");var subQ2=sQuery(id+"F0.wireOp",EDGE,"E1.top");var subQ3=sQuery(id+"F0.wireOp",EDGE,"E1.right");var subQ4=sQuery(id+"F0.wireOp",EDGE,"E7");Q15=makeQuery(id+"F6.opChamfer","BLEND_EDGE",EDGE,{"blendedFrom":[makeQuery(id+"F5.boolean.opBoolean","COPY",EDGE,{"derivedFrom":makeQuery(id+"F5.opExtrude","CAP_EDGE",EDGE,{"disambiguationData":[OSD([subQ0])],"isStart":true})}),makeQuery(id+"F5.boolean.opBoolean","SPLIT",FACE,{"disambiguationData":[TD([makeQuery(id+"F1.opExtrude","SWEPT_FACE",FACE,{"disambiguationData":[OSD([subQ3])]})])],"derivedFrom":makeQuery(id+"F1.opExtrude","CAP_FACE",FACE,{"disambiguationData":[OSD([subQ1,subQ2,sQuery(id+"F0.wireOp",EDGE,"E1.left"),subQ3,sQuery(id+"F0.wireOp",EDGE,"E3"),sQuery(id+"F0.wireOp",EDGE,"E5"),subQ4])],"isStart":false})})],"blendedInto":[makeQuery(id+"F5.boolean.opBoolean","SPLIT",FACE,{"disambiguationData":[TD([makeQuery(id+"F1.opExtrude","SWEPT_FACE",FACE,{"disambiguationData":[OSD([subQ3])]})])],"derivedFrom":makeQuery(id+"F1.opExtrude","CAP_FACE",FACE,{"disambiguationData":[OSD([subQ1,subQ2,sQuery(id+"F0.wireOp",EDGE,"E1.left"),subQ3,sQuery(id+"F0.wireOp",EDGE,"E3"),sQuery(id+"F0.wireOp",EDGE,"E5"),subQ4])],"isStart":false})})]});}
            var Q16;
            {var subQ0=sQuery(id+"F0.wireOp",EDGE,"E1.right");var subQ1=sQuery(id+"F0.wireOp",EDGE,"E1.bottom");var subQ2=sQuery(id+"F0.wireOp",EDGE,"E1.top");var subQ3=sQuery(id+"F0.wireOp",EDGE,"E7");Q16=makeQuery(id+"F6.opChamfer","BLEND_EDGE",EDGE,{"blendedFrom":[makeQuery(id+"F1.opExtrude","CAP_EDGE",EDGE,{"disambiguationData":[OSD([subQ0])],"isStart":false}),makeQuery(id+"F5.boolean.opBoolean","SPLIT",FACE,{"disambiguationData":[TD([makeQuery(id+"F1.opExtrude","SWEPT_FACE",FACE,{"disambiguationData":[OSD([subQ0])]})])],"derivedFrom":makeQuery(id+"F1.opExtrude","CAP_FACE",FACE,{"disambiguationData":[OSD([subQ1,subQ2,sQuery(id+"F0.wireOp",EDGE,"E1.left"),subQ0,sQuery(id+"F0.wireOp",EDGE,"E3"),sQuery(id+"F0.wireOp",EDGE,"E5"),subQ3])],"isStart":false})})],"blendedInto":[makeQuery(id+"F5.boolean.opBoolean","SPLIT",FACE,{"disambiguationData":[TD([makeQuery(id+"F1.opExtrude","SWEPT_FACE",FACE,{"disambiguationData":[OSD([subQ0])]})])],"derivedFrom":makeQuery(id+"F1.opExtrude","CAP_FACE",FACE,{"disambiguationData":[OSD([subQ1,subQ2,sQuery(id+"F0.wireOp",EDGE,"E1.left"),subQ0,sQuery(id+"F0.wireOp",EDGE,"E3"),sQuery(id+"F0.wireOp",EDGE,"E5"),subQ3])],"isStart":false})})]});}
            var Q17;
            {var subQ0=sQuery(id+"F0.wireOp",EDGE,"E1.left");var subQ1=sQuery(id+"F0.wireOp",EDGE,"E1.bottom");var subQ2=sQuery(id+"F0.wireOp",EDGE,"E1.top");var subQ3=sQuery(id+"F0.wireOp",EDGE,"E5");Q17=makeQuery(id+"F6.opChamfer","BLEND_EDGE",EDGE,{"blendedFrom":[makeQuery(id+"F1.opExtrude","CAP_EDGE",EDGE,{"disambiguationData":[OSD([subQ0])],"isStart":false}),makeQuery(id+"F5.boolean.opBoolean","SPLIT",FACE,{"disambiguationData":[TD([makeQuery(id+"F1.opExtrude","SWEPT_FACE",FACE,{"disambiguationData":[OSD([subQ0])]})])],"derivedFrom":makeQuery(id+"F1.opExtrude","CAP_FACE",FACE,{"disambiguationData":[OSD([subQ1,subQ2,subQ0,sQuery(id+"F0.wireOp",EDGE,"E1.right"),sQuery(id+"F0.wireOp",EDGE,"E3"),subQ3,sQuery(id+"F0.wireOp",EDGE,"E7")])],"isStart":false})})],"blendedInto":[makeQuery(id+"F5.boolean.opBoolean","SPLIT",FACE,{"disambiguationData":[TD([makeQuery(id+"F1.opExtrude","SWEPT_FACE",FACE,{"disambiguationData":[OSD([subQ0])]})])],"derivedFrom":makeQuery(id+"F1.opExtrude","CAP_FACE",FACE,{"disambiguationData":[OSD([subQ1,subQ2,subQ0,sQuery(id+"F0.wireOp",EDGE,"E1.right"),sQuery(id+"F0.wireOp",EDGE,"E3"),subQ3,sQuery(id+"F0.wireOp",EDGE,"E7")])],"isStart":false})})]});}
            fillet(context, id + "F9", {"entities" : qUnion([Q0, Q1, Q2, Q3, Q4, Q5, Q6, Q7, Q8, Q9, Q10, Q11, Q12, Q13, Q14, Q15, Q16, Q17]), "radius" : 5 * mm, "tangentPropagation" : true, "allowEdgeOverflow" : false});
        }
    });
